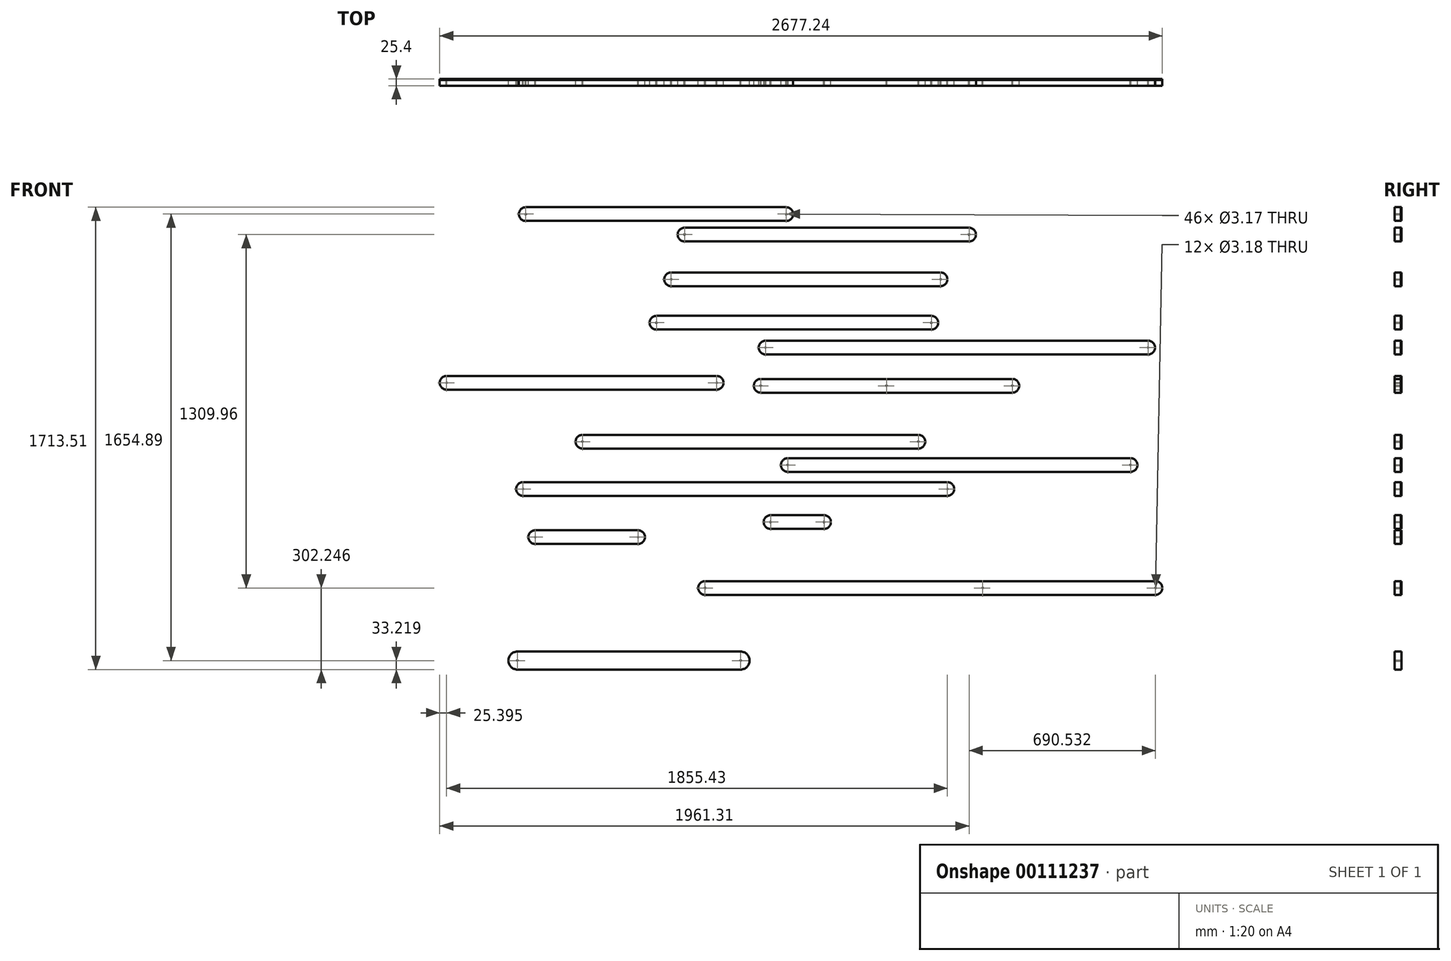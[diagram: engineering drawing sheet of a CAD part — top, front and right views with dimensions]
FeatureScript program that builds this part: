
annotation { "Feature Type Name" : "Feature", "Feature Type Description" : "" }
export const myFeature = defineFeature(function(context is Context, id is Id, definition is map)
    precondition{}
    {
        {
            var Q0;
            Q0=qCreatedBy(makeId("Front.planeOp"),FACE);
            var sketch = newSketch(context, id + "F0", { "sketchPlane" : qUnion([Q0])});
            skLineSegment(sketch, "E0", {"start": v(-76.1, 6.15) * mm, "end": v(922.12, 6.15) * mm});
            skLineSegment(sketch, "E1.MirrorCS", {"start": v(-76.1, -44.65) * mm, "end": v(922.12, -44.65) * mm});
            skArc(sketch, "E2", {"start": v(922.12, 6.15) * mm, "mid": v(947.52, -19.25) * mm, "end": v(922.12, -44.65) * mm});
            skArc(sketch, "E3", {"start": v(-76.1, -44.65) * mm, "mid": v(-101.5, -19.25) * mm, "end": v(-76.1, 6.15) * mm});
            skCircle(sketch, "E4", {"center": v(-76.1, -19.25) * mm, "radius": 1.59 * mm});
            skCircle(sketch, "E5", {"center": v(922.12, -19.25) * mm, "radius": 1.59 * mm});
            skLineSegment(sketch, "E6", {"start": v(-404.26, -595.63) * mm, "end": v(840.34, -595.63) * mm});
            skLineSegment(sketch, "E7.MirrorCS", {"start": v(-404.26, -646.43) * mm, "end": v(840.34, -646.43) * mm});
            skArc(sketch, "E8", {"start": v(840.34, -595.63) * mm, "mid": v(865.74, -621.03) * mm, "end": v(840.34, -646.43) * mm});
            skArc(sketch, "E9", {"start": v(-404.26, -646.43) * mm, "mid": v(-429.66, -621.03) * mm, "end": v(-404.26, -595.63) * mm});
            skCircle(sketch, "E10", {"center": v(-404.26, -621.03) * mm, "radius": 1.59 * mm});
            skCircle(sketch, "E11", {"center": v(840.34, -621.03) * mm, "radius": 1.59 * mm});
            skLineSegment(sketch, "E12", {"start": v(274.08, -246.76) * mm, "end": v(1691.4, -246.76) * mm});
            skLineSegment(sketch, "E13.MirrorCS", {"start": v(274.08, -297.56) * mm, "end": v(1691.4, -297.56) * mm});
            skArc(sketch, "E14", {"start": v(1691.4, -246.76) * mm, "mid": v(1716.8, -272.16) * mm, "end": v(1691.4, -297.56) * mm});
            skArc(sketch, "E15", {"start": v(274.08, -297.56) * mm, "mid": v(248.68, -272.16) * mm, "end": v(274.08, -246.76) * mm});
            skCircle(sketch, "E16", {"center": v(274.08, -272.16) * mm, "radius": 1.59 * mm});
            skCircle(sketch, "E17", {"center": v(1691.4, -272.16) * mm, "radius": 1.59 * mm});
            skLineSegment(sketch, "E18", {"start": v(-614.73, 247.92) * mm, "end": v(350.47, 247.92) * mm});
            skLineSegment(sketch, "E19.MirrorCS", {"start": v(-614.73, 197.12) * mm, "end": v(350.47, 197.12) * mm});
            skArc(sketch, "E20", {"start": v(350.47, 247.92) * mm, "mid": v(375.87, 222.52) * mm, "end": v(350.47, 197.12) * mm});
            skArc(sketch, "E21", {"start": v(-614.73, 197.12) * mm, "mid": v(-640.13, 222.52) * mm, "end": v(-614.73, 247.92) * mm});
            skCircle(sketch, "E22", {"center": v(-614.73, 222.52) * mm, "radius": 1.59 * mm});
            skCircle(sketch, "E23", {"center": v(350.47, 222.52) * mm, "radius": 1.59 * mm});
            skLineSegment(sketch, "E24", {"start": v(-26.22, 172.01) * mm, "end": v(1027.88, 172.01) * mm});
            skLineSegment(sketch, "E25.MirrorCS", {"start": v(-26.22, 121.21) * mm, "end": v(1027.88, 121.21) * mm});
            skArc(sketch, "E26", {"start": v(1027.88, 172.01) * mm, "mid": v(1053.28, 146.61) * mm, "end": v(1027.88, 121.21) * mm});
            skArc(sketch, "E27", {"start": v(-26.22, 121.21) * mm, "mid": v(-51.62, 146.61) * mm, "end": v(-26.22, 172.01) * mm});
            skCircle(sketch, "E28", {"center": v(-26.22, 146.61) * mm, "radius": 1.59 * mm});
            skCircle(sketch, "E29", {"center": v(1027.88, 146.61) * mm, "radius": 1.59 * mm});
            skLineSegment(sketch, "E30", {"start": v(-130.3, -154.66) * mm, "end": v(888.23, -154.66) * mm});
            skLineSegment(sketch, "E31.MirrorCS", {"start": v(-130.3, -205.46) * mm, "end": v(888.23, -205.46) * mm});
            skArc(sketch, "E32", {"start": v(888.23, -154.66) * mm, "mid": v(913.63, -180.06) * mm, "end": v(888.23, -205.46) * mm});
            skArc(sketch, "E33", {"start": v(-130.3, -205.46) * mm, "mid": v(-155.7, -180.06) * mm, "end": v(-130.3, -154.66) * mm});
            skCircle(sketch, "E34", {"center": v(-130.3, -180.06) * mm, "radius": 1.59 * mm});
            skCircle(sketch, "E35", {"center": v(888.23, -180.06) * mm, "radius": 1.59 * mm});
            skLineSegment(sketch, "E36", {"start": v(-908.03, -377.31) * mm, "end": v(92.73, -377.31) * mm});
            skLineSegment(sketch, "E37.MirrorCS", {"start": v(-908.03, -428.11) * mm, "end": v(92.73, -428.11) * mm});
            skArc(sketch, "E38", {"start": v(92.73, -377.31) * mm, "mid": v(118.13, -402.71) * mm, "end": v(92.73, -428.11) * mm});
            skArc(sketch, "E39", {"start": v(-908.03, -428.11) * mm, "mid": v(-933.43, -402.71) * mm, "end": v(-908.03, -377.31) * mm});
            skCircle(sketch, "E40", {"center": v(-908.03, -402.71) * mm, "radius": 1.59 * mm});
            skCircle(sketch, "E41", {"center": v(92.73, -402.71) * mm, "radius": 1.59 * mm});
            skLineSegment(sketch, "E42", {"start": v(49.63, -1137.94) * mm, "end": v(1718.41, -1137.94) * mm});
            skLineSegment(sketch, "E43.MirrorCS", {"start": v(49.63, -1188.74) * mm, "end": v(1718.41, -1188.74) * mm});
            skArc(sketch, "E44", {"start": v(1718.41, -1137.94) * mm, "mid": v(1743.81, -1163.34) * mm, "end": v(1718.41, -1188.74) * mm});
            skArc(sketch, "E45", {"start": v(49.63, -1188.74) * mm, "mid": v(24.23, -1163.34) * mm, "end": v(49.63, -1137.94) * mm});
            skCircle(sketch, "E46", {"center": v(49.63, -1163.34) * mm, "radius": 1.59 * mm});
            skCircle(sketch, "E47", {"center": v(1718.41, -1163.34) * mm, "radius": 1.59 * mm});
            skLineSegment(sketch, "E48", {"start": v(-624.86, -771) * mm, "end": v(947.4, -771) * mm});
            skLineSegment(sketch, "E49.MirrorCS", {"start": v(-624.86, -821.8) * mm, "end": v(947.4, -821.8) * mm});
            skArc(sketch, "E50", {"start": v(947.4, -771) * mm, "mid": v(972.8, -796.4) * mm, "end": v(947.4, -821.8) * mm});
            skArc(sketch, "E51", {"start": v(-624.86, -821.8) * mm, "mid": v(-650.26, -796.4) * mm, "end": v(-624.86, -771) * mm});
            skCircle(sketch, "E52", {"center": v(-624.86, -796.4) * mm, "radius": 1.59 * mm});
            skCircle(sketch, "E53", {"center": v(947.4, -796.4) * mm, "radius": 1.59 * mm});
            skLineSegment(sketch, "E54", {"start": v(292.53, -893.47) * mm, "end": v(490.65, -893.47) * mm});
            skLineSegment(sketch, "E55.MirrorCS", {"start": v(292.53, -944.27) * mm, "end": v(490.65, -944.27) * mm});
            skArc(sketch, "E56", {"start": v(490.65, -893.47) * mm, "mid": v(516.05, -918.87) * mm, "end": v(490.65, -944.27) * mm});
            skArc(sketch, "E57", {"start": v(292.53, -944.27) * mm, "mid": v(267.13, -918.87) * mm, "end": v(292.53, -893.47) * mm});
            skCircle(sketch, "E58", {"center": v(292.53, -918.87) * mm, "radius": 1.59 * mm});
            skCircle(sketch, "E59", {"center": v(490.65, -918.87) * mm, "radius": 1.59 * mm});
            skLineSegment(sketch, "E60", {"start": v(-579.38, -949.34) * mm, "end": v(-198.38, -949.34) * mm});
            skLineSegment(sketch, "E61.MirrorCS", {"start": v(-579.38, -1000.14) * mm, "end": v(-198.38, -1000.14) * mm});
            skArc(sketch, "E62", {"start": v(-198.38, -949.34) * mm, "mid": v(-172.98, -974.74) * mm, "end": v(-198.38, -1000.14) * mm});
            skArc(sketch, "E63", {"start": v(-579.38, -1000.14) * mm, "mid": v(-604.78, -974.74) * mm, "end": v(-579.38, -949.34) * mm});
            skCircle(sketch, "E64", {"center": v(-579.38, -974.74) * mm, "radius": 1.59 * mm});
            skCircle(sketch, "E65", {"center": v(-198.38, -974.74) * mm, "radius": 1.59 * mm});
            skLineSegment(sketch, "E66", {"start": v(356.25, -682.17) * mm, "end": v(1626.25, -682.17) * mm});
            skLineSegment(sketch, "E67.MirrorCS", {"start": v(356.25, -732.97) * mm, "end": v(1626.25, -732.97) * mm});
            skArc(sketch, "E68", {"start": v(1626.25, -682.17) * mm, "mid": v(1651.65, -707.57) * mm, "end": v(1626.25, -732.97) * mm});
            skArc(sketch, "E69", {"start": v(356.25, -732.97) * mm, "mid": v(330.85, -707.57) * mm, "end": v(356.25, -682.17) * mm});
            skCircle(sketch, "E70", {"center": v(356.25, -707.57) * mm, "radius": 1.59 * mm});
            skCircle(sketch, "E71", {"center": v(1626.25, -707.57) * mm, "radius": 1.59 * mm});
            skLineSegment(sketch, "E72", {"start": v(256.12, -388.4) * mm, "end": v(1188.3, -388.4) * mm});
            skLineSegment(sketch, "E73.MirrorCS", {"start": v(256.12, -439.2) * mm, "end": v(1188.3, -439.2) * mm});
            skArc(sketch, "E74", {"start": v(1188.3, -388.4) * mm, "mid": v(1213.7, -413.8) * mm, "end": v(1188.3, -439.2) * mm});
            skArc(sketch, "E75", {"start": v(256.12, -439.2) * mm, "mid": v(230.72, -413.8) * mm, "end": v(256.12, -388.4) * mm});
            skCircle(sketch, "E76", {"center": v(256.12, -413.8) * mm, "radius": 1.59 * mm});
            skCircle(sketch, "E77", {"center": v(1188.3, -413.8) * mm, "radius": 1.59 * mm});
            skCircle(sketch, "E78", {"center": v(722.21, -413.8) * mm, "radius": 1.59 * mm});
            skCircle(sketch, "E79", {"center": v(1078.12, -1163.34) * mm, "radius": 1.59 * mm});
            skLineSegment(sketch, "E80", {"start": v(-645.5, -1399.15) * mm, "end": v(181.6, -1399.15) * mm});
            skLineSegment(sketch, "E81", {"start": v(-645.5, -1465.6) * mm, "end": v(181.6, -1465.6) * mm});
            skArc(sketch, "E82", {"start": v(-645.5, -1465.6) * mm, "mid": v(-678.72, -1432.37) * mm, "end": v(-645.5, -1399.15) * mm});
            skArc(sketch, "E83", {"start": v(181.6, -1465.6) * mm, "mid": v(214.83, -1432.37) * mm, "end": v(181.6, -1399.15) * mm});
            skCircle(sketch, "E84", {"center": v(-645.5, -1432.37) * mm, "radius": 1.59 * mm});
            skCircle(sketch, "E85", {"center": v(181.6, -1432.37) * mm, "radius": 1.59 * mm});
            skSolve(sketch);
        }
        {
            var Q0;
            Q0=makeQuery(id+"F0.imprint","IMPRINT",FACE,{"disambiguationData":[TD([[makeQuery(id+"F0.imprint","IMPRINT",EDGE,{"derivedFrom":sQuery(id+"F0.wireOp",EDGE,"E0")}),-1.0]])]});
            var Q1;
            Q1=makeQuery(id+"F0.imprint","IMPRINT",FACE,{"disambiguationData":[TD([[makeQuery(id+"F0.imprint","IMPRINT",EDGE,{"derivedFrom":sQuery(id+"F0.wireOp",EDGE,"E42")}),-1.0]])]});
            var Q2;
            Q2=makeQuery(id+"F0.imprint","IMPRINT",FACE,{"disambiguationData":[TD([[makeQuery(id+"F0.imprint","IMPRINT",EDGE,{"derivedFrom":sQuery(id+"F0.wireOp",EDGE,"E18")}),-1.0]])]});
            var Q3;
            {var subQ0=sQuery(id+"F0.wireOp",EDGE,"E73.MirrorCS");Q3=makeQuery(id+"F0.imprint","IMPRINT",FACE,{"disambiguationData":[TD([[makeQuery(id+"F0.imprint","IMPRINT",EDGE,{"derivedFrom":subQ0}),1.0]])]});}
            var Q4;
            Q4=makeQuery(id+"F0.imprint","IMPRINT",FACE,{"disambiguationData":[TD([[makeQuery(id+"F0.imprint","IMPRINT",EDGE,{"derivedFrom":sQuery(id+"F0.wireOp",EDGE,"E12")}),-1.0]])]});
            var Q5;
            Q5=makeQuery(id+"F0.imprint","IMPRINT",FACE,{"disambiguationData":[TD([[makeQuery(id+"F0.imprint","IMPRINT",EDGE,{"derivedFrom":sQuery(id+"F0.wireOp",EDGE,"E66")}),-1.0]])]});
            var Q6;
            Q6=makeQuery(id+"F0.imprint","IMPRINT",FACE,{"disambiguationData":[TD([[makeQuery(id+"F0.imprint","IMPRINT",EDGE,{"derivedFrom":sQuery(id+"F0.wireOp",EDGE,"E48")}),-1.0]])]});
            var Q7;
            Q7=makeQuery(id+"F0.imprint","IMPRINT",FACE,{"disambiguationData":[TD([[makeQuery(id+"F0.imprint","IMPRINT",EDGE,{"derivedFrom":sQuery(id+"F0.wireOp",EDGE,"E60")}),-1.0]])]});
            var Q8;
            {var subQ7=sQuery(id+"F0.wireOp",EDGE,"E36");Q8=makeQuery(id+"F0.imprint","IMPRINT",FACE,{"disambiguationData":[TD([[makeQuery(id+"F0.imprint","IMPRINT",EDGE,{"derivedFrom":subQ7}),-1.0]])]});}
            var Q9;
            Q9=makeQuery(id+"F0.imprint","IMPRINT",FACE,{"disambiguationData":[TD([[makeQuery(id+"F0.imprint","IMPRINT",EDGE,{"derivedFrom":sQuery(id+"F0.wireOp",EDGE,"E54")}),-1.0]])]});
            var Q10;
            Q10=makeQuery(id+"F0.imprint","IMPRINT",FACE,{"disambiguationData":[TD([[makeQuery(id+"F0.imprint","IMPRINT",EDGE,{"derivedFrom":sQuery(id+"F0.wireOp",EDGE,"E24")}),-1.0]])]});
            var Q11;
            Q11=makeQuery(id+"F0.imprint","IMPRINT",FACE,{"disambiguationData":[TD([[makeQuery(id+"F0.imprint","IMPRINT",EDGE,{"derivedFrom":sQuery(id+"F0.wireOp",EDGE,"E6")}),-1.0]])]});
            var Q12;
            Q12=makeQuery(id+"F0.imprint","IMPRINT",FACE,{"disambiguationData":[TD([[makeQuery(id+"F0.imprint","IMPRINT",EDGE,{"derivedFrom":sQuery(id+"F0.wireOp",EDGE,"E30")}),-1.0]])]});
            extrude(context, id + "F1", {"entities" : qUnion([Q0, Q1, Q2, Q3, Q4, Q5, Q6, Q7, Q8, Q9, Q10, Q11, Q12]), "depth" : 3.17 * mm});
        }
        {
            var Q0;
            Q0 = qSketchRegion(id + "F0", true);
            extrude(context, id + "F2", {"entities" : qUnion([Q0]), "depth" : 25.4 * mm});
        }
    });
